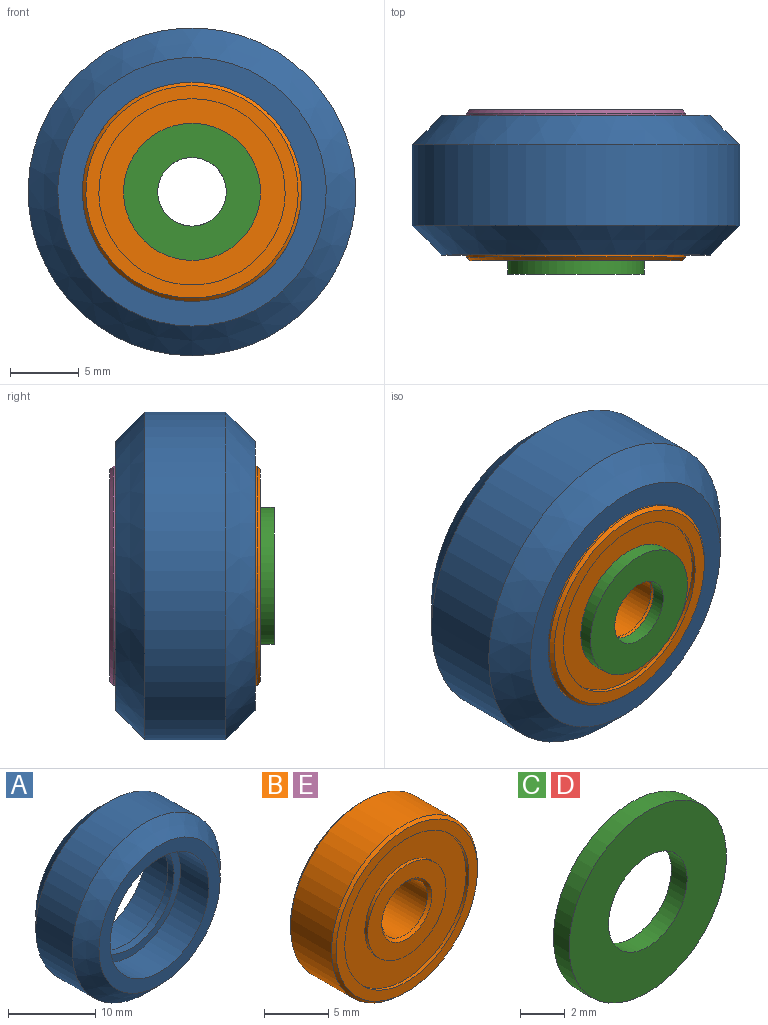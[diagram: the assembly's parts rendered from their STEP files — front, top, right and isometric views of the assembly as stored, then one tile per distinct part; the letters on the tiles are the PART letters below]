
ASSEMBLY  parts=5 mates=4
PART A: 10 faces, bbox 23.9x10.2x23.9 mm
  f0: plane 19.6x19.6mm, normal (0,-1,0), area 101.3mm2, adj f1,f9
  f1: cylinder r=7.99mm len=15.98mm, axis (0,-1,0), area 230.9mm2, adj f0,f2
  f2: plane 15.98x15.98mm, normal (0,-1,0), area 48.8mm2, adj f1,f3
  f3: cylinder r=6.95mm len=13.9mm, axis (0,-1,0), area 43.7mm2, adj f2,f4
  f4: plane 15.98x15.98mm, normal (0,1,0), area 48.8mm2, adj f3,f5
  f5: cylinder r=7.99mm len=15.98mm, axis (0,-1,0), area 230.9mm2, adj f4,f6
  f6: plane 19.6x19.6mm, normal (0,1,0), area 101.3mm2, adj f5,f7
  f7: cone r=9.8mm half-angle=45.1deg, axis (0,-1,0), area 208.3mm2, adj f6,f8
  f8: cylinder r=11.96mm len=23.92mm, axis (0,-1,0), area 443.4mm2, adj f7,f9
  f9: cone r=9.8mm half-angle=45.1deg, axis (0,1,0), area 208.3mm2, adj f0,f8
PART B: 16 faces, bbox 16x5x16 mm
  f0: plane 13.6x13.6mm, normal (0,-1,0), area 87.2mm2, adj f1,f11
  f1: cylinder r=4.3mm len=8.6mm, axis (0,1,0), area 8.1mm2, adj f0,f2
  f2: plane 8.6x8.6mm, normal (0,-1,0), area 34.3mm2, adj f1,f13
  f3: cylinder r=2.5mm len=5mm, axis (0,1,0), area 70.7mm2, adj f12,f13
  f4: plane 8.6x8.6mm, normal (0,1,0), area 34.3mm2, adj f5,f12
  f5: cylinder r=4.3mm len=8.6mm, axis (0,1,0), area 8.1mm2, adj f4,f6
  f6: plane 13.6x13.6mm, normal (0,1,0), area 87.2mm2, adj f5,f7
  f7: cylinder r=6.8mm len=13.6mm, axis (0,1,0), area 12.8mm2, adj f6,f8
  f8: plane 15.5x15.5mm, normal (0,1,0), area 43.4mm2, adj f7,f14
  f9: cylinder r=8mm len=16mm, axis (0,1,0), area 226.2mm2, adj f14,f15
  f10: plane 15.5x15.5mm, normal (0,-1,0), area 43.4mm2, adj f11,f15
  f11: cylinder r=6.8mm len=13.6mm, axis (0,1,0), area 12.8mm2, adj f0,f10
  f12: cone r=2.5mm half-angle=45deg, axis (0,1,0), area 5.8mm2, adj f3,f4
  f13: cone r=2.75mm half-angle=45deg, axis (0,-1,0), area 5.8mm2, adj f2,f3
  f14: cone r=7.75mm half-angle=45deg, axis (0,-1,0), area 17.5mm2, adj f8,f9
  f15: cone r=8mm half-angle=45deg, axis (0,1,0), area 17.5mm2, adj f9,f10
PART C: 4 faces, bbox 10x1x10 mm
  f0: cylinder r=2.5mm len=5mm, axis (0,1,0), area 15.7mm2, adj f2,f3
  f1: cylinder r=5mm len=10mm, axis (0,1,0), area 31.4mm2, adj f2,f3
  f2: plane 10x10mm, normal (0,-1,0), area 58.9mm2, adj f0,f1
  f3: plane 10x10mm, normal (0,1,0), area 58.9mm2, adj f0,f1
PART D: same geometry as C
PART E: same geometry as B
PLACE A at identity
PLACE B at identity
PLACE C t=(0,-6,0)mm
PLACE D at identity
PLACE E t=(0,6,0)mm
MATE revolute A.f1 <-> D.f0  axis (0,-1,0) through (0,0,0)mm
MATE fastened E.f1 <-> D.f0  axis (0,-1,0) through (0,0.5,0)mm
MATE fastened D.f0 <-> B.f1  axis (0,1,0) through (0,-0.5,0)mm
MATE fastened C.f0 <-> B.f1  axis (0,-1,0) through (0,-5.5,0)mm
